# Revit family: RA-NCX_Double Angle_Left_DN15_RFA_1
name_source: partatom
category: Pipe Accessories
units: mm (PartAtom-declared; Revit-internal decimal feet)

## family parameters
Always vertical = Yes
Cut with Voids When Loaded = No
OmniClass Number = 23.65.55.14.17
OmniClass Title = Adjusting/Controlling Valves for Liquid Services
Part Type = Valve - Breaks Into
Round Connector Dimension = Use Diameter
Shared = No
Work Plane-Based = No

## types (1)
- RA-NCX_Double Angle_Left_DN15_013G4240
    Connection = Internal Thread
    D = 15 mm  [stored 0.0492126 ft]
    DB4 = 25 mm  [stored 0.082021 ft]
    Description = Thermostatic Radiator Valve
    H = 64 mm
    H1 = 8 mm  [stored 0.0262467 ft]
    HH = 22 mm  [stored 0.0721785 ft]
    Ha = 47 mm  [stored 0.154199 ft]
    IfcExportAs = IfcValveType
    IfcExportType = RA-NCX
    Kvs = 0.9 m³/h
    L = 73 mm
    L1 = 23 mm
    L2 = 5 mm  [stored 0.0164042 ft]
    L3 = 3 mm  [stored 0.00984252 ft]
    L4 = 10 mm  [stored 0.0328084 ft]
    L5 = 32 mm  [stored 0.104987 ft]
    L6 = 16 mm  [stored 0.0524934 ft]
    LOD 200 = No
    LOD 350 = Yes
    LT1 = 27 mm  [stored 0.0885827 ft]
    LT2 = 30 mm  [stored 0.0984252 ft]
    La = 58 mm  [stored 0.190289 ft]
    Manufacturer = Danfoss
    Max Differential Pressure = 0.6 bar
    Max Medium Temperature = 120 ˚C
    Max Operating Pressure = 10 bar
    Model = 013G4240
    Model Type = RA-NCX_Double Angle_Left_DN15
    RB1 = 11 mm  [stored 0.0360892 ft]
    RB2 = 13 mm
    RB3 = 11 mm  [stored 0.0360892 ft]
    RV1 = 13 mm
    RV2 = 13 mm
    RV3 = 15 mm  [stored 0.0492126 ft]
    RV4 = 11 mm  [stored 0.0360892 ft]
    R_200 = 15 mm  [stored 0.0492126 ft]
    R_200_1 = 17 mm
    Setting Range = 1-7,N
    TD = 31 mm
    URL = https://store.danfoss.com
    Valve Body Material = Danfoss Brass (Chrome plated)
    W = 49 mm
    Wa = 32 mm  [stored 0.104987 ft]
    Weight = 0.31 kg

note: [stored X ft] marks values corroborated as IEEE doubles in the binary element streams (Revit-internal decimal feet)

## geometry (parser evidence)
native form markers: Sweep x2
no freeform markers — native parametric forms only
